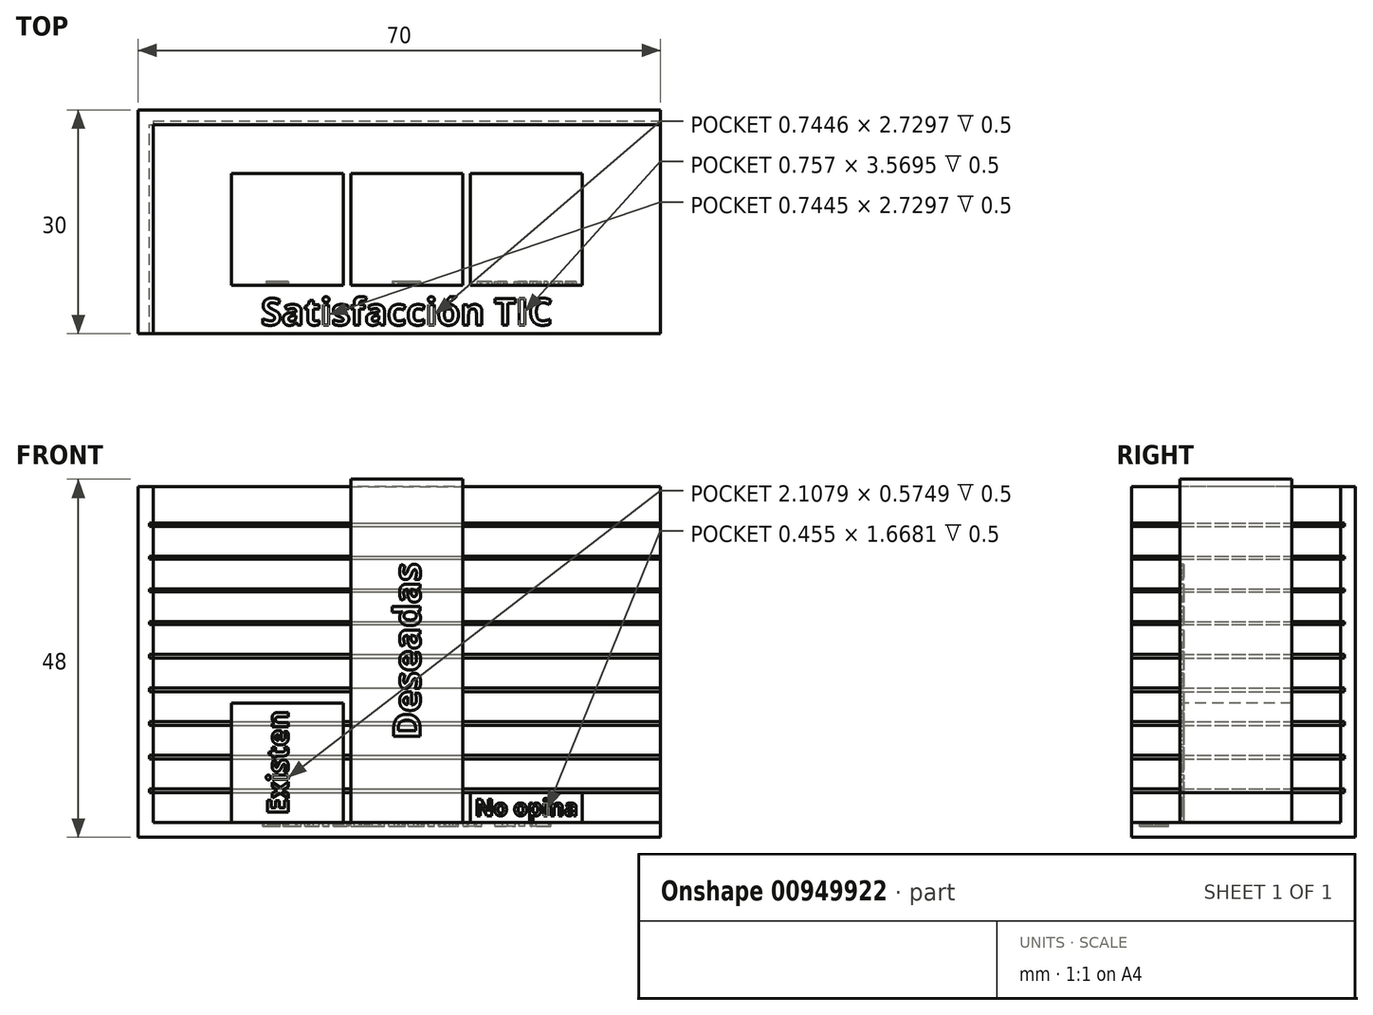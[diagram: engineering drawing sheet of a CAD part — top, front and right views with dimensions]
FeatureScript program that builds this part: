
annotation { "Feature Type Name" : "Feature", "Feature Type Description" : "" }
export const myFeature = defineFeature(function(context is Context, id is Id, definition is map)
    precondition{}
    {
        {
            var Q0;
            Q0=qCreatedBy(makeId("Top.planeOp"),FACE);
            var sketch = newSketch(context, id + "F0", { "sketchPlane" : qUnion([Q0])});
            skLineSegment(sketch, "E0.bottom", {"start": v(-35, 15) * mm, "end": v(35, 15) * mm});
            skLineSegment(sketch, "E0.top", {"start": v(-35, -15) * mm, "end": v(35, -15) * mm});
            skLineSegment(sketch, "E0.left", {"start": v(-35, 15) * mm, "end": v(-35, -15) * mm});
            skLineSegment(sketch, "E0.right", {"start": v(35, 15) * mm, "end": v(35, -15) * mm});
            skPoint(sketch, "E0.middle", {"position": v(0, 0) * mm});
            skSolve(sketch);
        }
        {
            var Q0;
            Q0=qSketchRegion(id+"F0",true);
            extrude(context, id + "F1", {"entities" : qUnion([Q0]), "depth" : 2 * mm, "offsetDistance" : 25 * mm});
        }
        {
            var Q0;
            Q0=makeQuery(id+"F1.opExtrude","SWEPT_FACE",FACE,{"disambiguationData":[OSD([sQuery(id+"F0.wireOp",EDGE,"E0.bottom")])]});
            cPlane(context, id + "F2", {"entities" : qUnion([Q0]), "cplaneType" : CPlaneType.OFFSET, "offset" : 0 * mm, "width" : 150 * mm, "height" : 150 * mm});
        }
        {
            var Q0;
            Q0=makeQuery(id+"F1.opExtrude","SWEPT_FACE",FACE,{"disambiguationData":[OSD([sQuery(id+"F0.wireOp",EDGE,"E0.left")])]});
            cPlane(context, id + "F3", {"entities" : qUnion([Q0]), "cplaneType" : CPlaneType.OFFSET, "offset" : 0 * mm, "width" : 150 * mm, "height" : 150 * mm});
        }
        {
            var Q0;
            Q0=qCreatedBy(id+"F3.planeOp",FACE);
            var sketch = newSketch(context, id + "F4", { "sketchPlane" : qUnion([Q0])});
            skLineSegment(sketch, "E1.bottom", {"start": v(-15, 2) * mm, "end": v(15, 2) * mm});
            skLineSegment(sketch, "E1.top", {"start": v(-15, 47) * mm, "end": v(15, 47) * mm});
            skLineSegment(sketch, "E1.left", {"start": v(-15, 2) * mm, "end": v(-15, 47) * mm});
            skLineSegment(sketch, "E1.right", {"start": v(15, 2) * mm, "end": v(15, 47) * mm});
            skSolve(sketch);
        }
        {
            var Q0;
            Q0=qCreatedBy(id+"F2.planeOp",FACE);
            var sketch = newSketch(context, id + "F5", { "sketchPlane" : qUnion([Q0])});
            skLineSegment(sketch, "E2.bottom", {"start": v(35, 2) * mm, "end": v(-35, 2) * mm});
            skLineSegment(sketch, "E2.top", {"start": v(35, 47) * mm, "end": v(-35, 47) * mm});
            skLineSegment(sketch, "E2.left", {"start": v(35, 2) * mm, "end": v(35, 47) * mm});
            skLineSegment(sketch, "E2.right", {"start": v(-35, 2) * mm, "end": v(-35, 47) * mm});
            skSolve(sketch);
        }
        {
            var Q0;
            Q0=qSketchRegion(id+"F4",true);
            extrude(context, id + "F6", {"entities" : qUnion([Q0]), "oppositeDirection" : true, "depth" : 2 * mm, "offsetDistance" : 25 * mm});
        }
        {
            var Q0;
            Q0=qSketchRegion(id+"F5",true);
            extrude(context, id + "F7", {"entities" : qUnion([Q0]), "operationType" : NewBodyOperationType.ADD, "oppositeDirection" : true, "depth" : 2 * mm, "offsetDistance" : 25 * mm});
        }
        {
            var Q0;
            Q0=makeQuery(id+"F6.opExtrude","CAP_FACE",FACE,{"disambiguationData":[OSD([sQuery(id+"F4.wireOp",EDGE,"E1.bottom"),sQuery(id+"F4.wireOp",EDGE,"E1.top"),sQuery(id+"F4.wireOp",EDGE,"E1.left"),sQuery(id+"F4.wireOp",EDGE,"E1.right")])],"isStart":false});
            var sketch = newSketch(context, id + "F8", { "sketchPlane" : qUnion([Q0])});
            skLineSegment(sketch, "E3.bottom", {"start": v(-15, 6.5) * mm, "end": v(13, 6.5) * mm});
            skLineSegment(sketch, "E3.top", {"start": v(-15, 6) * mm, "end": v(13, 6) * mm});
            skLineSegment(sketch, "E3.left", {"start": v(-15, 6.5) * mm, "end": v(-15, 6) * mm});
            skLineSegment(sketch, "E3.right", {"start": v(13, 6.5) * mm, "end": v(13, 6) * mm});
            skLineSegment(sketch, "E4.bottom", {"start": v(-15, 11) * mm, "end": v(13, 11) * mm});
            skLineSegment(sketch, "E4.top", {"start": v(-15, 10.5) * mm, "end": v(13, 10.5) * mm});
            skLineSegment(sketch, "E4.left", {"start": v(-15, 11) * mm, "end": v(-15, 10.5) * mm});
            skLineSegment(sketch, "E4.right", {"start": v(13, 11) * mm, "end": v(13, 10.5) * mm});
            skLineSegment(sketch, "E5.bottom", {"start": v(-15, 15.5) * mm, "end": v(13, 15.5) * mm});
            skLineSegment(sketch, "E5.top", {"start": v(-15, 15) * mm, "end": v(13, 15) * mm});
            skLineSegment(sketch, "E5.left", {"start": v(-15, 15.5) * mm, "end": v(-15, 15) * mm});
            skLineSegment(sketch, "E5.right", {"start": v(13, 15.5) * mm, "end": v(13, 15) * mm});
            skLineSegment(sketch, "E6.bottom", {"start": v(-15, 20) * mm, "end": v(13, 20) * mm});
            skLineSegment(sketch, "E6.top", {"start": v(-15, 19.5) * mm, "end": v(13, 19.5) * mm});
            skLineSegment(sketch, "E6.left", {"start": v(-15, 20) * mm, "end": v(-15, 19.5) * mm});
            skLineSegment(sketch, "E6.right", {"start": v(13, 20) * mm, "end": v(13, 19.5) * mm});
            skLineSegment(sketch, "E7.bottom", {"start": v(-15, 24.5) * mm, "end": v(13, 24.5) * mm});
            skLineSegment(sketch, "E7.top", {"start": v(-15, 24) * mm, "end": v(13, 24) * mm});
            skLineSegment(sketch, "E7.left", {"start": v(-15, 24.5) * mm, "end": v(-15, 24) * mm});
            skLineSegment(sketch, "E7.right", {"start": v(13, 24.5) * mm, "end": v(13, 24) * mm});
            skLineSegment(sketch, "E8.bottom", {"start": v(-15, 28.9) * mm, "end": v(13, 28.9) * mm});
            skLineSegment(sketch, "E8.top", {"start": v(-15, 28.5) * mm, "end": v(13, 28.5) * mm});
            skLineSegment(sketch, "E8.left", {"start": v(-15, 28.9) * mm, "end": v(-15, 28.5) * mm});
            skLineSegment(sketch, "E8.right", {"start": v(13, 28.9) * mm, "end": v(13, 28.5) * mm});
            skLineSegment(sketch, "E9.bottom", {"start": v(-15, 33.3) * mm, "end": v(13, 33.3) * mm});
            skLineSegment(sketch, "E9.top", {"start": v(-15, 32.9) * mm, "end": v(13, 32.9) * mm});
            skLineSegment(sketch, "E9.left", {"start": v(-15, 33.3) * mm, "end": v(-15, 32.9) * mm});
            skLineSegment(sketch, "E9.right", {"start": v(13, 33.3) * mm, "end": v(13, 32.9) * mm});
            skLineSegment(sketch, "E10.bottom", {"start": v(-15, 37.7) * mm, "end": v(13, 37.7) * mm});
            skLineSegment(sketch, "E10.top", {"start": v(-15, 37.3) * mm, "end": v(13, 37.3) * mm});
            skLineSegment(sketch, "E10.left", {"start": v(-15, 37.7) * mm, "end": v(-15, 37.3) * mm});
            skLineSegment(sketch, "E10.right", {"start": v(13, 37.7) * mm, "end": v(13, 37.3) * mm});
            skLineSegment(sketch, "E11.bottom", {"start": v(-15, 42.1) * mm, "end": v(13, 42.1) * mm});
            skLineSegment(sketch, "E11.top", {"start": v(-15, 41.7) * mm, "end": v(13, 41.7) * mm});
            skLineSegment(sketch, "E11.left", {"start": v(-15, 42.1) * mm, "end": v(-15, 41.7) * mm});
            skLineSegment(sketch, "E11.right", {"start": v(13, 42.1) * mm, "end": v(13, 41.7) * mm});
            skSolve(sketch);
        }
        {
            var Q0;
            Q0=qSketchRegion(id+"F8",true);
            extrude(context, id + "F9", {"entities" : qUnion([Q0]), "operationType" : NewBodyOperationType.REMOVE, "oppositeDirection" : true, "depth" : 0.5 * mm, "offsetDistance" : 25 * mm});
        }
        {
            var Q0;
            Q0=makeQuery(id+"F9.boolean.opBoolean","MERGE",FACE,{"derivedFrom":[makeQuery(id+"F7.opExtrude","CAP_FACE",FACE,{"disambiguationData":[OSD([sQuery(id+"F5.wireOp",EDGE,"E2.bottom"),sQuery(id+"F5.wireOp",EDGE,"E2.top"),sQuery(id+"F5.wireOp",EDGE,"E2.left"),sQuery(id+"F5.wireOp",EDGE,"E2.right")])],"isStart":false})],"fromTools":[makeQuery(id+"F9.opExtrude","SWEPT_FACE",FACE,{"disambiguationData":[OSD([sQuery(id+"F8.wireOp",EDGE,"E3.right")])]}),makeQuery(id+"F9.opExtrude","SWEPT_FACE",FACE,{"disambiguationData":[OSD([sQuery(id+"F8.wireOp",EDGE,"E4.right")])]}),makeQuery(id+"F9.opExtrude","SWEPT_FACE",FACE,{"disambiguationData":[OSD([sQuery(id+"F8.wireOp",EDGE,"E5.right")])]}),makeQuery(id+"F9.opExtrude","SWEPT_FACE",FACE,{"disambiguationData":[OSD([sQuery(id+"F8.wireOp",EDGE,"E6.right")])]}),makeQuery(id+"F9.opExtrude","SWEPT_FACE",FACE,{"disambiguationData":[OSD([sQuery(id+"F8.wireOp",EDGE,"E7.right")])]}),makeQuery(id+"F9.opExtrude","SWEPT_FACE",FACE,{"disambiguationData":[OSD([sQuery(id+"F8.wireOp",EDGE,"E8.right")])]}),makeQuery(id+"F9.opExtrude","SWEPT_FACE",FACE,{"disambiguationData":[OSD([sQuery(id+"F8.wireOp",EDGE,"E9.right")])]}),makeQuery(id+"F9.opExtrude","SWEPT_FACE",FACE,{"disambiguationData":[OSD([sQuery(id+"F8.wireOp",EDGE,"E10.right")])]}),makeQuery(id+"F9.opExtrude","SWEPT_FACE",FACE,{"disambiguationData":[OSD([sQuery(id+"F8.wireOp",EDGE,"E11.right")])]})]});
            var sketch = newSketch(context, id + "F10", { "sketchPlane" : qUnion([Q0])});
            skLineSegment(sketch, "E12.bottom", {"start": v(-33, 6.5) * mm, "end": v(35, 6.5) * mm});
            skLineSegment(sketch, "E12.top", {"start": v(-33, 6) * mm, "end": v(35, 6) * mm});
            skLineSegment(sketch, "E12.left", {"start": v(-33, 6.5) * mm, "end": v(-33, 6) * mm});
            skLineSegment(sketch, "E12.right", {"start": v(35, 6.5) * mm, "end": v(35, 6) * mm});
            skLineSegment(sketch, "E13.bottom", {"start": v(-33, 11) * mm, "end": v(35, 11) * mm});
            skLineSegment(sketch, "E13.top", {"start": v(-33, 10.5) * mm, "end": v(35, 10.5) * mm});
            skLineSegment(sketch, "E13.left", {"start": v(-33, 11) * mm, "end": v(-33, 10.5) * mm});
            skLineSegment(sketch, "E13.right", {"start": v(35, 11) * mm, "end": v(35, 10.5) * mm});
            skLineSegment(sketch, "E14.bottom", {"start": v(-33, 15.5) * mm, "end": v(35, 15.5) * mm});
            skLineSegment(sketch, "E14.top", {"start": v(-33, 15) * mm, "end": v(35, 15) * mm});
            skLineSegment(sketch, "E14.left", {"start": v(-33, 15.5) * mm, "end": v(-33, 15) * mm});
            skLineSegment(sketch, "E14.right", {"start": v(35, 15.5) * mm, "end": v(35, 15) * mm});
            skLineSegment(sketch, "E15.bottom", {"start": v(-33, 20) * mm, "end": v(35, 20) * mm});
            skLineSegment(sketch, "E15.top", {"start": v(-33, 19.5) * mm, "end": v(35, 19.5) * mm});
            skLineSegment(sketch, "E15.left", {"start": v(-33, 20) * mm, "end": v(-33, 19.5) * mm});
            skLineSegment(sketch, "E15.right", {"start": v(35, 20) * mm, "end": v(35, 19.5) * mm});
            skLineSegment(sketch, "E16.bottom", {"start": v(-33, 24.5) * mm, "end": v(35, 24.5) * mm});
            skLineSegment(sketch, "E16.top", {"start": v(-33, 24) * mm, "end": v(35, 24) * mm});
            skLineSegment(sketch, "E16.left", {"start": v(-33, 24.5) * mm, "end": v(-33, 24) * mm});
            skLineSegment(sketch, "E16.right", {"start": v(35, 24.5) * mm, "end": v(35, 24) * mm});
            skLineSegment(sketch, "E17.bottom", {"start": v(-33, 28.9) * mm, "end": v(35, 28.9) * mm});
            skLineSegment(sketch, "E17.top", {"start": v(-33, 28.5) * mm, "end": v(35, 28.5) * mm});
            skLineSegment(sketch, "E17.left", {"start": v(-33, 28.9) * mm, "end": v(-33, 28.5) * mm});
            skLineSegment(sketch, "E17.right", {"start": v(35, 28.9) * mm, "end": v(35, 28.5) * mm});
            skLineSegment(sketch, "E18.bottom", {"start": v(-33, 33.3) * mm, "end": v(35, 33.3) * mm});
            skLineSegment(sketch, "E18.top", {"start": v(-33, 32.9) * mm, "end": v(35, 32.9) * mm});
            skLineSegment(sketch, "E18.left", {"start": v(-33, 33.3) * mm, "end": v(-33, 32.9) * mm});
            skLineSegment(sketch, "E18.right", {"start": v(35, 33.3) * mm, "end": v(35, 32.9) * mm});
            skLineSegment(sketch, "E19.bottom", {"start": v(-33, 37.7) * mm, "end": v(35, 37.7) * mm});
            skLineSegment(sketch, "E19.top", {"start": v(-33, 37.3) * mm, "end": v(35, 37.3) * mm});
            skLineSegment(sketch, "E19.left", {"start": v(-33, 37.7) * mm, "end": v(-33, 37.3) * mm});
            skLineSegment(sketch, "E19.right", {"start": v(35, 37.7) * mm, "end": v(35, 37.3) * mm});
            skLineSegment(sketch, "E20.bottom", {"start": v(-33, 42.1) * mm, "end": v(35, 42.1) * mm});
            skLineSegment(sketch, "E20.top", {"start": v(-33, 41.7) * mm, "end": v(35, 41.7) * mm});
            skLineSegment(sketch, "E20.left", {"start": v(-33, 42.1) * mm, "end": v(-33, 41.7) * mm});
            skLineSegment(sketch, "E20.right", {"start": v(35, 42.1) * mm, "end": v(35, 41.7) * mm});
            skSolve(sketch);
        }
        {
            var Q0;
            Q0=makeQuery(id+"F1.opExtrude","CAP_FACE",FACE,{"disambiguationData":[OSD([sQuery(id+"F0.wireOp",EDGE,"E0.bottom"),sQuery(id+"F0.wireOp",EDGE,"E0.top"),sQuery(id+"F0.wireOp",EDGE,"E0.left"),sQuery(id+"F0.wireOp",EDGE,"E0.right")])],"isStart":false});
            var sketch = newSketch(context, id + "F11", { "sketchPlane" : qUnion([Q0])});
            skLineSegment(sketch, "E21.bottom", {"start": v(-22.5, 6.5) * mm, "end": v(-7.5, 6.5) * mm});
            skLineSegment(sketch, "E21.top", {"start": v(-22.5, -8.5) * mm, "end": v(-7.5, -8.5) * mm});
            skLineSegment(sketch, "E21.left", {"start": v(-22.5, 6.5) * mm, "end": v(-22.5, -8.5) * mm});
            skLineSegment(sketch, "E21.right", {"start": v(-7.5, 6.5) * mm, "end": v(-7.5, -8.5) * mm});
            skLineSegment(sketch, "E22.left", {"start": v(-7.5, 6.5) * mm, "end": v(-7.5, -7) * mm});
            skLineSegment(sketch, "E23.bottom", {"start": v(-6.5, 6.5) * mm, "end": v(8.5, 6.5) * mm});
            skLineSegment(sketch, "E23.top", {"start": v(-6.5, -8.5) * mm, "end": v(8.5, -8.5) * mm});
            skLineSegment(sketch, "E23.left", {"start": v(-6.5, 6.5) * mm, "end": v(-6.5, -8.5) * mm});
            skLineSegment(sketch, "E23.right", {"start": v(8.5, 6.5) * mm, "end": v(8.5, -8.5) * mm});
            skLineSegment(sketch, "E24", {"start": v(1, 6.5) * mm, "end": v(1, -8.5) * mm, "construction": true});
            skLineSegment(sketch, "E25.bottom", {"start": v(9.5, 6.5) * mm, "end": v(24.5, 6.5) * mm});
            skLineSegment(sketch, "E25.top", {"start": v(9.5, -8.5) * mm, "end": v(24.5, -8.5) * mm});
            skLineSegment(sketch, "E25.left", {"start": v(9.5, 6.5) * mm, "end": v(9.5, -8.5) * mm});
            skLineSegment(sketch, "E25.right", {"start": v(24.5, 6.5) * mm, "end": v(24.5, -8.5) * mm});
            skLineSegment(sketch, "E26", {"start": v(-22.5, -1) * mm, "end": v(24.5, -1) * mm, "construction": true});
            skSolve(sketch);
        }
        {
            var Q0;
            Q0=qSketchRegion(id+"F10",true);
            extrude(context, id + "F12", {"entities" : qUnion([Q0]), "operationType" : NewBodyOperationType.REMOVE, "oppositeDirection" : true, "depth" : 0.5 * mm, "offsetDistance" : 25 * mm});
        }
        {
            var Q0;
            Q0=makeQuery(id+"F11.imprint","IMPRINT",FACE,{"disambiguationData":[TD([[makeQuery(id+"F11.imprint","IMPRINT",EDGE,{"derivedFrom":sQuery(id+"F11.wireOp",EDGE,"E21.bottom")}),-1.0]])]});
            extrude(context, id + "F13", {"entities" : qUnion([Q0]), "operationType" : NewBodyOperationType.ADD, "depth" : 16 * mm, "offsetDistance" : 25 * mm});
        }
        {
            var Q0;
            Q0=makeQuery(id+"F11.imprint","IMPRINT",FACE,{"disambiguationData":[TD([[makeQuery(id+"F11.imprint","IMPRINT",EDGE,{"derivedFrom":sQuery(id+"F11.wireOp",EDGE,"E23.bottom")}),-1.0]])]});
            extrude(context, id + "F14", {"entities" : qUnion([Q0]), "operationType" : NewBodyOperationType.ADD, "depth" : 46 * mm, "offsetDistance" : 25 * mm});
        }
        {
            var Q0;
            Q0=makeQuery(id+"F11.imprint","IMPRINT",FACE,{"disambiguationData":[TD([[makeQuery(id+"F11.imprint","IMPRINT",EDGE,{"derivedFrom":sQuery(id+"F11.wireOp",EDGE,"E25.bottom")}),-1.0]])]});
            extrude(context, id + "F15", {"entities" : qUnion([Q0]), "operationType" : NewBodyOperationType.ADD, "depth" : 4 * mm, "offsetDistance" : 25 * mm});
        }
        {
            var Q0;
            Q0=makeQuery(id+"F11.imprint","IMPRINT",FACE,{"disambiguationData":[TD([[makeQuery(id+"F11.imprint","IMPRINT",EDGE,{"derivedFrom":sQuery(id+"F11.wireOp",EDGE,"E21.bottom")}),1.0]])]});
            var sketch = newSketch(context, id + "F16", { "sketchPlane" : qUnion([Q0])});
            skText(sketch, "E27", { "text": "Satisfacción TIC ", "fontName": "OpenSans-Bold.ttf"});
            const initialGuessF16  = {"E27": [-0.01853, -0.01384, 1, 0, 0.0036]};
            skSetInitialGuess(sketch, initialGuessF16);
            skSolve(sketch);
        }
        {
            var Q0;
            Q0 = qSketchRegion(id + "F16", true);
            extrude(context, id + "F17", {"entities" : qUnion([Q0]), "operationType" : NewBodyOperationType.REMOVE, "oppositeDirection" : true, "depth" : 0.5 * mm, "offsetDistance" : 25 * mm});
        }
        {
            var Q0;
            Q0=makeQuery(id+"F13.opExtrude","SWEPT_FACE",FACE,{"disambiguationData":[OSD([sQuery(id+"F11.wireOp",EDGE,"E21.top")])]});
            var sketch = newSketch(context, id + "F18", { "sketchPlane" : qUnion([Q0])});
            skText(sketch, "E28", { "text": "Existen\n", "fontName": "OpenSans-Bold.ttf"});
            const initialGuessF18  = {"E28": [-0.0149, 0.00304, 0, 1, 0.00278]};
            skSetInitialGuess(sketch, initialGuessF18);
            skSolve(sketch);
        }
        {
            var Q0;
            Q0 = qSketchRegion(id + "F18", true);
            extrude(context, id + "F19", {"entities" : qUnion([Q0]), "operationType" : NewBodyOperationType.REMOVE, "oppositeDirection" : true, "depth" : 0.5 * mm, "offsetDistance" : 25 * mm});
        }
        {
            var Q0;
            Q0=makeQuery(id+"F14.opExtrude","SWEPT_FACE",FACE,{"disambiguationData":[OSD([sQuery(id+"F11.wireOp",EDGE,"E23.top")])]});
            var sketch = newSketch(context, id + "F20", { "sketchPlane" : qUnion([Q0])});
            skText(sketch, "E29", { "text": "Deseadas", "fontName": "OpenSans-Bold.ttf"});
            skLineSegment(sketch, "E30", {"start": v(1, 13.08) * mm, "end": v(1, 36.92) * mm, "construction": true});
            const initialGuessF20  = {"E29": [0.0028, 0.01308, 0, 1, 0.00359]};
            skSetInitialGuess(sketch, initialGuessF20);
            skSolve(sketch);
        }
        {
            var Q0;
            Q0 = qSketchRegion(id + "F20", true);
            extrude(context, id + "F21", {"entities" : qUnion([Q0]), "operationType" : NewBodyOperationType.REMOVE, "oppositeDirection" : true, "depth" : 0.5 * mm, "offsetDistance" : 25 * mm});
        }
        {
            var Q0;
            Q0=makeQuery(id+"F15.opExtrude","SWEPT_FACE",FACE,{"disambiguationData":[OSD([sQuery(id+"F11.wireOp",EDGE,"E25.top")])]});
            var sketch = newSketch(context, id + "F22", { "sketchPlane" : qUnion([Q0])});
            skText(sketch, "E31", { "text": "No opina", "fontName": "OpenSans-Bold.ttf"});
            skLineSegment(sketch, "E32", {"start": v(10.13, 4) * mm, "end": v(23.87, 4) * mm, "construction": true});
            const initialGuessF22  = {"E31": [0.01013, 0.0029, 1, 0, 0.0022]};
            skSetInitialGuess(sketch, initialGuessF22);
            skSolve(sketch);
        }
        {
            var Q0;
            Q0 = qSketchRegion(id + "F22", true);
            extrude(context, id + "F23", {"entities" : qUnion([Q0]), "operationType" : NewBodyOperationType.REMOVE, "oppositeDirection" : true, "depth" : 0.5 * mm, "offsetDistance" : 25 * mm});
        }
    });
